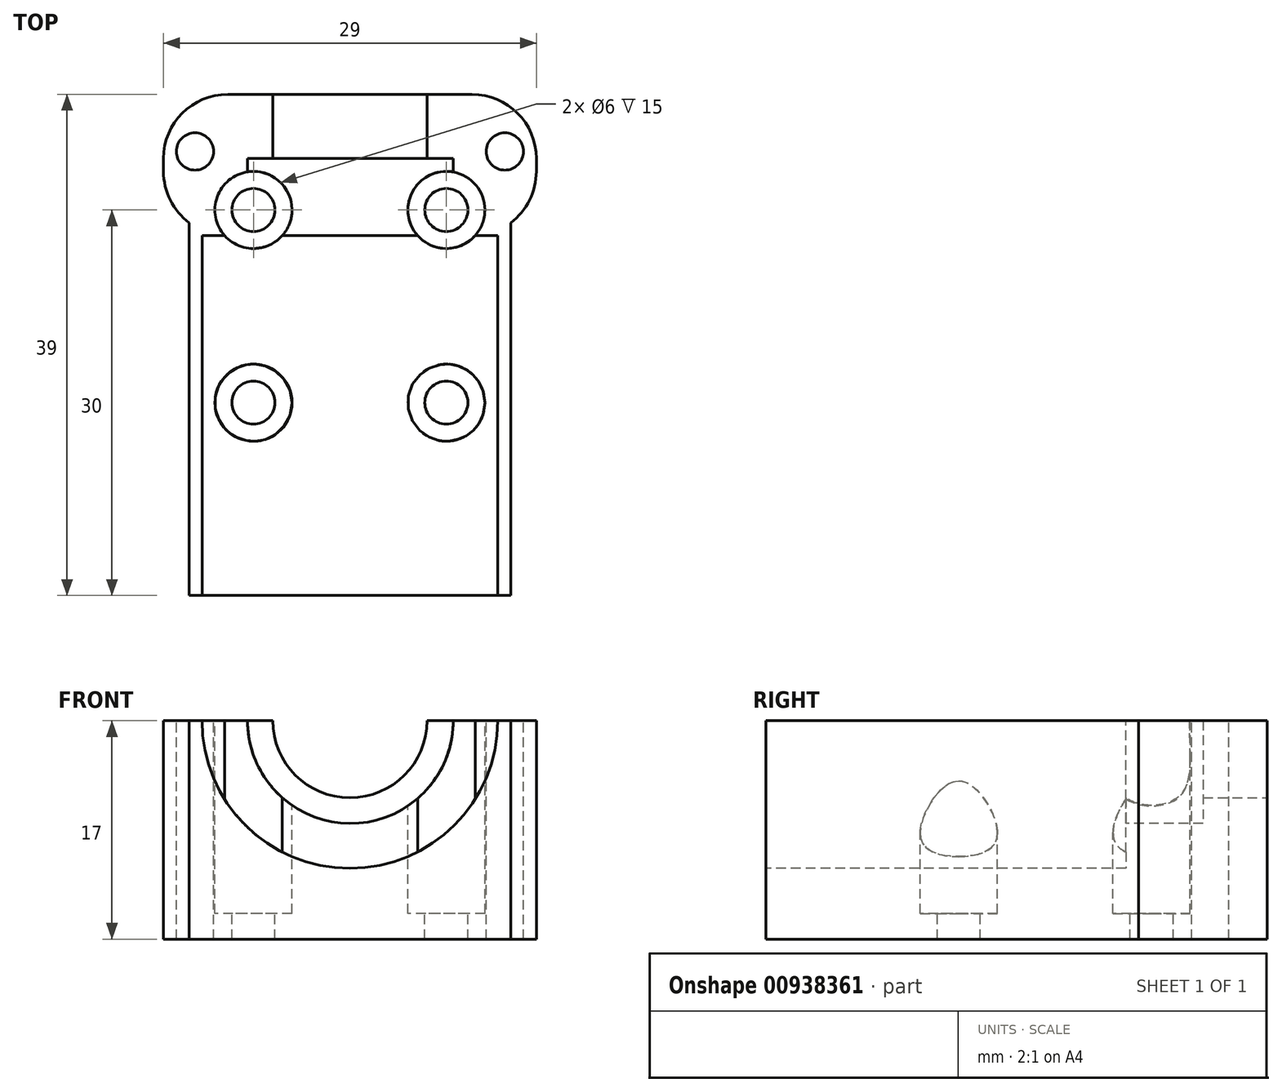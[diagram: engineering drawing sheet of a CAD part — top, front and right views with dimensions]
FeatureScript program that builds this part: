
annotation { "Feature Type Name" : "Feature", "Feature Type Description" : "" }
export const myFeature = defineFeature(function(context is Context, id is Id, definition is map)
    precondition{}
    {
        {
            var Q0;
            Q0=qCreatedBy(makeId("Top.planeOp"),FACE);
            var sketch = newSketch(context, id + "F0", { "sketchPlane" : qUnion([Q0])});
            skLineSegment(sketch, "E0.bottom", {"start": v(0, 0) * mm, "end": v(25, 0) * mm});
            skLineSegment(sketch, "E0.top", {"start": v(0, 30) * mm, "end": v(25, 30) * mm});
            skLineSegment(sketch, "E0.left", {"start": v(0, 0) * mm, "end": v(0, 30) * mm});
            skLineSegment(sketch, "E0.right", {"start": v(25, 0) * mm, "end": v(25, 30) * mm});
            skSolve(sketch);
        }
        {
            var Q0;
            Q0=qSketchRegion(id+"F0",true);
            extrude(context, id + "F1", {"entities" : qUnion([Q0]), "depth" : 4 * mm});
        }
        {
            var Q0;
            Q0=makeQuery(id+"F1.opExtrude","CAP_FACE",FACE,{"disambiguationData":[OSD([sQuery(id+"F0.wireOp",EDGE,"E0.bottom"),sQuery(id+"F0.wireOp",EDGE,"E0.top"),sQuery(id+"F0.wireOp",EDGE,"E0.left"),sQuery(id+"F0.wireOp",EDGE,"E0.right")])],"isStart":false});
            var sketch = newSketch(context, id + "F2", { "sketchPlane" : qUnion([Q0])});
            skLineSegment(sketch, "E1.bottom", {"start": v(0, 30) * mm, "end": v(25, 30) * mm});
            skLineSegment(sketch, "E1.top", {"start": v(0, 19) * mm, "end": v(25, 19) * mm});
            skLineSegment(sketch, "E1.left", {"start": v(0, 30) * mm, "end": v(0, 19) * mm});
            skLineSegment(sketch, "E1.right", {"start": v(25, 30) * mm, "end": v(25, 19) * mm});
            skSolve(sketch);
        }
        {
            var Q0;
            Q0=qSketchRegion(id+"F2",true);
            extrude(context, id + "F3", {"entities" : qUnion([Q0]), "operationType" : NewBodyOperationType.ADD, "depth" : 13 * mm});
        }
        {
            var Q0;
            Q0=makeQuery(id+"F1.opExtrude","CAP_FACE",FACE,{"disambiguationData":[OSD([sQuery(id+"F0.wireOp",EDGE,"E0.bottom"),sQuery(id+"F0.wireOp",EDGE,"E0.top"),sQuery(id+"F0.wireOp",EDGE,"E0.left"),sQuery(id+"F0.wireOp",EDGE,"E0.right")])],"isStart":false});
            var sketch = newSketch(context, id + "F4", { "sketchPlane" : qUnion([Q0])});
            skCircle(sketch, "E2", {"center": v(5, 21) * mm, "radius": 1.68 * mm});
            skCircle(sketch, "E3", {"center": v(20, 21) * mm, "radius": 1.68 * mm});
            skCircle(sketch, "E4", {"center": v(5, 6) * mm, "radius": 1.68 * mm});
            skCircle(sketch, "E5", {"center": v(20, 6) * mm, "radius": 1.68 * mm});
            skCircle(sketch, "E6", {"center": v(5, 21) * mm, "radius": 3 * mm});
            skCircle(sketch, "E7", {"center": v(20, 21) * mm, "radius": 3 * mm});
            skCircle(sketch, "E8", {"center": v(5, 6) * mm, "radius": 3 * mm});
            skCircle(sketch, "E9", {"center": v(20, 6) * mm, "radius": 3 * mm});
            skSolve(sketch);
        }
        {
            var Q0;
            Q0=makeQuery(id+"F4.imprint","IMPRINT",FACE,{"disambiguationData":[TD([[makeQuery(id+"F4.imprint","IMPRINT",EDGE,{"derivedFrom":sQuery(id+"F4.wireOp",EDGE,"E2")}),1.0]])]});
            var Q1;
            Q1=makeQuery(id+"F4.imprint","IMPRINT",FACE,{"disambiguationData":[TD([[makeQuery(id+"F4.imprint","IMPRINT",EDGE,{"derivedFrom":sQuery(id+"F4.wireOp",EDGE,"E3")}),1.0]])]});
            var Q2;
            Q2=makeQuery(id+"F4.imprint","IMPRINT",FACE,{"disambiguationData":[TD([[makeQuery(id+"F4.imprint","IMPRINT",EDGE,{"derivedFrom":sQuery(id+"F4.wireOp",EDGE,"E5")}),1.0]])]});
            var Q3;
            Q3=makeQuery(id+"F4.imprint","IMPRINT",FACE,{"disambiguationData":[TD([[makeQuery(id+"F4.imprint","IMPRINT",EDGE,{"derivedFrom":sQuery(id+"F4.wireOp",EDGE,"E4")}),1.0]])]});
            var Q4;
            {var subQ0=sQuery(id+"F4.wireOp",EDGE,"E2");var subQ1=makeQuery(id+"F3.opExtrude","CAP_EDGE",EDGE,{"disambiguationData":[OSD([sQuery(id+"F2.wireOp",EDGE,"E1.top")])],"isStart":true});var subQ2=makeQuery(id+"F4.imprint","INTERSECT",VERTEX,{"disambiguationData":[OD(0.0)],"derivedFrom":[subQ1,subQ0]});Q4=makeQuery(id+"F4.imprint","IMPRINT",FACE,{"disambiguationData":[TD([[makeQuery(id+"F4.imprint","IMPRINT",EDGE,{"disambiguationData":[TD([[subQ2,1.0]])],"derivedFrom":subQ0}),1.0]])]});}
            extrude(context, id + "F5", {"entities" : qUnion([Q0, Q1, Q2, Q3, Q4]), "operationType" : NewBodyOperationType.REMOVE, "oppositeDirection" : true, "depth" : 25 * mm, "hasSecondDirection" : true, "secondDirectionOppositeDirection" : false, "secondDirectionDepth" : 25 * mm});
        }
        {
            var Q0;
            Q0=makeQuery(id+"F3.boolean.opBoolean","MERGE",FACE,{"derivedFrom":[makeQuery(id+"F1.opExtrude","SWEPT_FACE",FACE,{"disambiguationData":[OSD([sQuery(id+"F0.wireOp",EDGE,"E0.top")])]}),makeQuery(id+"F3.opExtrude","SWEPT_FACE",FACE,{"disambiguationData":[OSD([sQuery(id+"F2.wireOp",EDGE,"E1.bottom")])]})]});
            var sketch = newSketch(context, id + "F6", { "sketchPlane" : qUnion([Q0])});
            skCircle(sketch, "E10", {"center": v(-12.5, 17) * mm, "radius": 6 * mm});
            skSolve(sketch);
        }
        {
            var Q0;
            {var subQ0=makeQuery(id+"F3.opExtrude","CAP_EDGE",EDGE,{"disambiguationData":[OSD([sQuery(id+"F2.wireOp",EDGE,"E1.bottom")])],"isStart":false});var subQ1=sQuery(id+"F6.wireOp",EDGE,"E10");var subQ3=makeQuery(id+"F6.imprint","INTERSECT",VERTEX,{"disambiguationData":[OD(0.0)],"derivedFrom":[subQ0,subQ1]});Q0=makeQuery(id+"F6.imprint","IMPRINT",FACE,{"disambiguationData":[TD([[makeQuery(id+"F6.imprint","IMPRINT",EDGE,{"disambiguationData":[TD([[subQ3,1.0]])],"derivedFrom":subQ1}),1.0]])]});}
            extrude(context, id + "F7", {"entities" : qUnion([Q0]), "operationType" : NewBodyOperationType.REMOVE, "oppositeDirection" : true, "depth" : 6 * mm});
        }
        {
            var Q0;
            Q0=makeQuery(id+"F3.opExtrude","SWEPT_FACE",FACE,{"disambiguationData":[OSD([sQuery(id+"F2.wireOp",EDGE,"E1.top")])]});
            var sketch = newSketch(context, id + "F8", { "sketchPlane" : qUnion([Q0])});
            skCircle(sketch, "E11", {"center": v(12.54, 17) * mm, "radius": 8 * mm});
            skSolve(sketch);
        }
        {
            var Q0;
            Q0=qSketchRegion(id+"F8",true);
            extrude(context, id + "F9", {"entities" : qUnion([Q0]), "operationType" : NewBodyOperationType.REMOVE, "oppositeDirection" : true, "depth" : 6 * mm, "offsetDistance" : 25 * mm});
        }
        {
            var Q0;
            Q0=makeQuery(id+"F4.imprint","IMPRINT",FACE,{"disambiguationData":[TD([[makeQuery(id+"F4.imprint","IMPRINT",EDGE,{"derivedFrom":sQuery(id+"F4.wireOp",EDGE,"E2")}),-1.0]])]});
            var Q1;
            Q1=makeQuery(id+"F4.imprint","IMPRINT",FACE,{"disambiguationData":[TD([[makeQuery(id+"F4.imprint","IMPRINT",EDGE,{"derivedFrom":sQuery(id+"F4.wireOp",EDGE,"E3")}),-1.0]])]});
            var Q2;
            Q2=makeQuery(id+"F4.imprint","IMPRINT",FACE,{"disambiguationData":[TD([[makeQuery(id+"F4.imprint","IMPRINT",EDGE,{"derivedFrom":sQuery(id+"F4.wireOp",EDGE,"E5")}),-1.0]])]});
            var Q3;
            Q3=makeQuery(id+"F4.imprint","IMPRINT",FACE,{"disambiguationData":[TD([[makeQuery(id+"F4.imprint","IMPRINT",EDGE,{"derivedFrom":sQuery(id+"F4.wireOp",EDGE,"E4")}),-1.0]])]});
            var Q4;
            {var subQ0=sQuery(id+"F4.wireOp",EDGE,"E7");var subQ1=makeQuery(id+"F3.opExtrude","CAP_EDGE",EDGE,{"disambiguationData":[OSD([sQuery(id+"F2.wireOp",EDGE,"E1.top")])],"isStart":true});var subQ2=makeQuery(id+"F4.imprint","INTERSECT",VERTEX,{"disambiguationData":[OD(0.0)],"derivedFrom":[subQ1,subQ0]});Q4=makeQuery(id+"F4.imprint","IMPRINT",FACE,{"disambiguationData":[TD([[makeQuery(id+"F4.imprint","IMPRINT",EDGE,{"disambiguationData":[TD([[subQ2,1.0]])],"derivedFrom":subQ0}),1.0]])]});}
            var Q5;
            {var subQ0=sQuery(id+"F4.wireOp",EDGE,"E6");var subQ1=makeQuery(id+"F3.opExtrude","CAP_EDGE",EDGE,{"disambiguationData":[OSD([sQuery(id+"F2.wireOp",EDGE,"E1.top")])],"isStart":true});var subQ2=makeQuery(id+"F4.imprint","INTERSECT",VERTEX,{"disambiguationData":[OD(0.0)],"derivedFrom":[subQ1,subQ0]});Q5=makeQuery(id+"F4.imprint","IMPRINT",FACE,{"disambiguationData":[TD([[makeQuery(id+"F4.imprint","IMPRINT",EDGE,{"disambiguationData":[TD([[subQ2,-1.0]])],"derivedFrom":subQ0}),1.0]])]});}
            extrude(context, id + "F10", {"entities" : qUnion([Q0, Q1, Q2, Q3, Q4, Q5]), "operationType" : NewBodyOperationType.REMOVE, "oppositeDirection" : true, "depth" : 2 * mm, "hasSecondDirection" : true, "secondDirectionOppositeDirection" : false, "secondDirectionDepth" : 25 * mm, "offsetDistance" : 25 * mm});
        }
        {
            var Q0;
            Q0=makeQuery(id+"F3.boolean.opBoolean","MERGE",FACE,{"derivedFrom":[makeQuery(id+"F1.opExtrude","SWEPT_FACE",FACE,{"disambiguationData":[OSD([sQuery(id+"F0.wireOp",EDGE,"E0.left")])]}),makeQuery(id+"F3.opExtrude","SWEPT_FACE",FACE,{"disambiguationData":[OSD([sQuery(id+"F2.wireOp",EDGE,"E1.left")])]})]});
            var sketch = newSketch(context, id + "F11", { "sketchPlane" : qUnion([Q0])});
            skLineSegment(sketch, "E12.bottom", {"start": v(-30, 0) * mm, "end": v(-19, 0) * mm});
            skLineSegment(sketch, "E12.top", {"start": v(-30, 17) * mm, "end": v(-19, 17) * mm});
            skLineSegment(sketch, "E12.left", {"start": v(-30, 0) * mm, "end": v(-30, 17) * mm});
            skLineSegment(sketch, "E12.right", {"start": v(-19, 0) * mm, "end": v(-19, 17) * mm});
            skSolve(sketch);
        }
        {
            var Q0;
            {var subQ3=sQuery(id+"F11.wireOp",EDGE,"E12.bottom");Q0=makeQuery(id+"F11.imprint","IMPRINT",FACE,{"disambiguationData":[TD([[makeQuery(id+"F11.imprint","IMPRINT",EDGE,{"derivedFrom":subQ3}),-1.0]])]});}
            extrude(context, id + "F12", {"entities" : qUnion([Q0]), "operationType" : NewBodyOperationType.ADD, "depth" : 2 * mm});
        }
        {
            var Q0;
            Q0=makeQuery(id+"F3.boolean.opBoolean","MERGE",FACE,{"derivedFrom":[makeQuery(id+"F1.opExtrude","SWEPT_FACE",FACE,{"disambiguationData":[OSD([sQuery(id+"F0.wireOp",EDGE,"E0.right")])]}),makeQuery(id+"F3.opExtrude","SWEPT_FACE",FACE,{"disambiguationData":[OSD([sQuery(id+"F2.wireOp",EDGE,"E1.right")])]})]});
            var sketch = newSketch(context, id + "F13", { "sketchPlane" : qUnion([Q0])});
            skLineSegment(sketch, "E13.bottom", {"start": v(30, 0) * mm, "end": v(19, 0) * mm});
            skLineSegment(sketch, "E13.top", {"start": v(30, 17) * mm, "end": v(19, 17) * mm});
            skLineSegment(sketch, "E13.left", {"start": v(30, 0) * mm, "end": v(30, 17) * mm});
            skLineSegment(sketch, "E13.right", {"start": v(19, 0) * mm, "end": v(19, 17) * mm});
            skSolve(sketch);
        }
        {
            var Q0;
            Q0=qSketchRegion(id+"F13",true);
            extrude(context, id + "F14", {"entities" : qUnion([Q0]), "operationType" : NewBodyOperationType.ADD, "depth" : 2 * mm});
        }
        {
            var Q0;
            {var subQ0=sQuery(id+"F2.wireOp",EDGE,"E1.bottom");var subQ1=sQuery(id+"F2.wireOp",EDGE,"E1.top");var subQ2=sQuery(id+"F2.wireOp",EDGE,"E1.left");Q0=makeQuery(id+"F9.boolean.opBoolean","SPLIT",FACE,{"disambiguationData":[TD([makeQuery(id+"F1.opExtrude","SWEPT_FACE",FACE,{"disambiguationData":[OSD([sQuery(id+"F0.wireOp",EDGE,"E0.left")])]})])],"derivedFrom":makeQuery(id+"F3.opExtrude","CAP_FACE",FACE,{"disambiguationData":[OSD([subQ0,subQ1,subQ2,sQuery(id+"F2.wireOp",EDGE,"E1.right")])],"isStart":false})});}
            var sketch = newSketch(context, id + "F15", { "sketchPlane" : qUnion([Q0])});
            skCircle(sketch, "E14", {"center": v(0.45, 25.55) * mm, "radius": 1.45 * mm});
            skCircle(sketch, "E15", {"center": v(24.55, 25.55) * mm, "radius": 1.45 * mm});
            skSolve(sketch);
        }
        {
            var Q0;
            Q0=qSketchRegion(id+"F15",true);
            extrude(context, id + "F16", {"entities" : qUnion([Q0]), "operationType" : NewBodyOperationType.REMOVE, "oppositeDirection" : true, "depth" : 25 * mm});
        }
        {
            var Q0;
            Q0=makeQuery(id+"F12.opExtrude","CAP_EDGE",EDGE,{"disambiguationData":[OSD([sQuery(id+"F11.wireOp",EDGE,"E12.right")])],"isStart":false});
            var Q1;
            Q1=makeQuery(id+"F12.opExtrude","CAP_EDGE",EDGE,{"disambiguationData":[OSD([sQuery(id+"F11.wireOp",EDGE,"E12.left")])],"isStart":false});
            var Q2;
            Q2=makeQuery(id+"F14.opExtrude","CAP_EDGE",EDGE,{"disambiguationData":[OSD([sQuery(id+"F13.wireOp",EDGE,"E13.left")])],"isStart":false});
            var Q3;
            Q3=makeQuery(id+"F14.opExtrude","CAP_EDGE",EDGE,{"disambiguationData":[OSD([sQuery(id+"F13.wireOp",EDGE,"E13.right")])],"isStart":false});
            fillet(context, id + "F17", {"entities" : qUnion([Q0, Q1, Q2, Q3]), "radius" : 5 * mm, "tangentPropagation" : true, "allowEdgeOverflow" : false});
        }
        {
            var Q0;
            Q0=makeQuery(id+"F1.opExtrude","SWEPT_FACE",FACE,{"disambiguationData":[OSD([sQuery(id+"F0.wireOp",EDGE,"E0.bottom")])]});
            extrude(context, id + "F18", {"entities" : qUnion([Q0]), "operationType" : NewBodyOperationType.ADD, "depth" : 9 * mm, "offsetDistance" : 25 * mm});
        }
        {
            var Q0;
            {var subQ0=sQuery(id+"F0.wireOp",EDGE,"E0.bottom");Q0=makeQuery(id+"F18.boolean.opBoolean","MERGE",FACE,{"derivedFrom":[makeQuery(id+"F1.opExtrude","CAP_FACE",FACE,{"disambiguationData":[OSD([subQ0,sQuery(id+"F0.wireOp",EDGE,"E0.top"),sQuery(id+"F0.wireOp",EDGE,"E0.left"),sQuery(id+"F0.wireOp",EDGE,"E0.right")])],"isStart":false}),makeQuery(id+"F18.opExtrude","SWEPT_FACE",FACE,{"disambiguationData":[OSD([subQ0]),TDD([makeQuery(id+"F1.opExtrude","CAP_EDGE",EDGE,{"disambiguationData":[OSD([subQ0])],"isStart":false})])]})]});}
            extrude(context, id + "F19", {"entities" : qUnion([Q0]), "operationType" : NewBodyOperationType.ADD, "depth" : 13 * mm, "offsetDistance" : 25 * mm});
        }
        {
            var Q0;
            {var subQ0=sQuery(id+"F0.wireOp",EDGE,"E0.bottom");Q0=makeQuery(id+"F19.boolean.opBoolean","MERGE",FACE,{"derivedFrom":[makeQuery(id+"F18.opExtrude","CAP_FACE",FACE,{"disambiguationData":[OSD([subQ0])],"isStart":false}),makeQuery(id+"F19.opExtrude","SWEPT_FACE",FACE,{"disambiguationData":[OSD([subQ0])]})]});}
            var sketch = newSketch(context, id + "F20", { "sketchPlane" : qUnion([Q0])});
            skCircle(sketch, "E16", {"center": v(12.5, 17) * mm, "radius": 11.5 * mm});
            skSolve(sketch);
        }
        {
            var Q0;
            {var subQ0=sQuery(id+"F20.wireOp",EDGE,"E16");var subQ1=makeQuery(id+"F19.opExtrude","CAP_EDGE",EDGE,{"disambiguationData":[OSD([sQuery(id+"F0.wireOp",EDGE,"E0.bottom")])],"isStart":false});var subQ2=makeQuery(id+"F20.imprint","INTERSECT",VERTEX,{"disambiguationData":[OD(0.0)],"derivedFrom":[subQ1,subQ0]});Q0=makeQuery(id+"F20.imprint","IMPRINT",FACE,{"disambiguationData":[TD([[makeQuery(id+"F20.imprint","IMPRINT",EDGE,{"disambiguationData":[TD([[subQ2,-1.0]])],"derivedFrom":subQ0}),1.0]])]});}
            var Q1;
            Q1=makeQuery(id+"F19.opExtrude","SWEPT_FACE",FACE,{"disambiguationData":[OSD([sQuery(id+"F2.wireOp",EDGE,"E1.top")])]});
            extrude(context, id + "F21", {"entities" : qUnion([Q0]), "operationType" : NewBodyOperationType.REMOVE, "endBound" : BoundingType.UP_TO_SURFACE, "oppositeDirection" : true, "depth" : 44 * mm, "endBoundEntityFace" : qUnion([Q1]), "offsetDistance" : 25 * mm});
        }
    });
